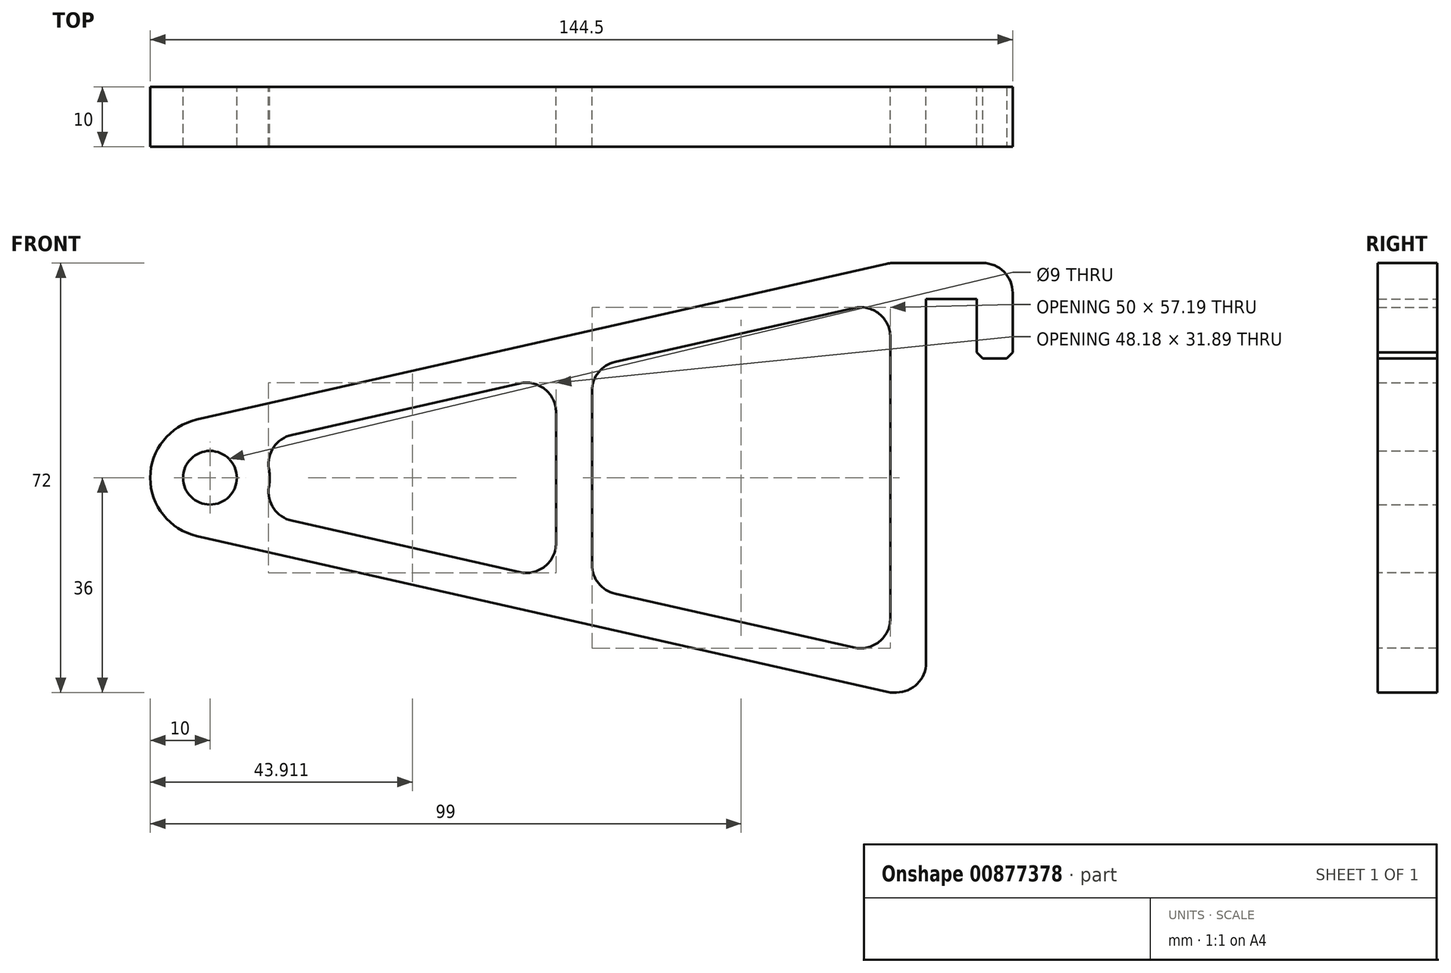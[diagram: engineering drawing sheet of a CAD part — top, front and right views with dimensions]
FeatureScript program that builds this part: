
annotation { "Feature Type Name" : "Feature", "Feature Type Description" : "" }
export const myFeature = defineFeature(function(context is Context, id is Id, definition is map)
    precondition{}
    {
        {
            var Q0;
            Q0=qCreatedBy(makeId("Front.planeOp"),FACE);
            var sketch = newSketch(context, id + "F0", { "sketchPlane" : qUnion([Q0])});
            skLineSegment(sketch, "E0", {"start": v(0, 0) * mm, "end": v(-120, 0) * mm, "construction": true});
            skLineSegment(sketch, "E1", {"start": v(0, 0) * mm, "end": v(0, 30) * mm});
            skLineSegment(sketch, "E2.MirrorCS", {"start": v(0, 0) * mm, "end": v(0, -36) * mm});
            skArc(sketch, "E3", {"start": v(-122.2, 9.75) * mm, "mid": v(-130, 0) * mm, "end": v(-122.2, -9.75) * mm});
            skCircle(sketch, "E4", {"center": v(-120, 0) * mm, "radius": 4.5 * mm});
            skLineSegment(sketch, "E5", {"start": v(0, -36) * mm, "end": v(-6, -36) * mm});
            skLineSegment(sketch, "E6", {"start": v(-6, -36) * mm, "end": v(-122.2, -9.75) * mm});
            skLineSegment(sketch, "E7.MirrorCS", {"start": v(0, 36) * mm, "end": v(-6, 36) * mm});
            skLineSegment(sketch, "E8.MirrorCS", {"start": v(-6, 36) * mm, "end": v(-122.2, 9.75) * mm});
            skLineSegment(sketch, "E9", {"start": v(-6, 29.85) * mm, "end": v(-6, -29.85) * mm});
            skLineSegment(sketch, "E10", {"start": v(-56, 18.56) * mm, "end": v(-56, -18.56) * mm});
            skLineSegment(sketch, "E11.0", {"start": v(-62, 17.2) * mm, "end": v(-62, -17.2) * mm});
            skLineSegment(sketch, "E12.0", {"start": v(-6, 29.85) * mm, "end": v(-56, 18.56) * mm});
            skLineSegment(sketch, "E13.MirrorCS", {"start": v(-6, -29.85) * mm, "end": v(-56, -18.56) * mm});
            skPoint(sketch, "E14.orphan", {"position": v(-120.88, 3.9) * mm});
            skPoint(sketch, "E15.orphan", {"position": v(-120.88, -3.9) * mm});
            skArc(sketch, "E16.trimOffspring", {"start": v(-111.94, -5.92) * mm, "mid": v(-110, 0) * mm, "end": v(-111.94, 5.92) * mm});
            skLineSegment(sketch, "E17.trimOffspring", {"start": v(-62, -17.2) * mm, "end": v(-111.94, -5.92) * mm});
            skLineSegment(sketch, "E18.trimOffspring", {"start": v(-62, 17.2) * mm, "end": v(-111.94, 5.92) * mm});
            skPoint(sketch, "E19.orphan", {"position": v(-4.68, 30.15) * mm});
            skPoint(sketch, "E20.orphan", {"position": v(-4.68, -30.15) * mm});
            skLineSegment(sketch, "E21", {"start": v(0, 36) * mm, "end": v(8.5, 36) * mm});
            skLineSegment(sketch, "E22", {"start": v(8.5, 30) * mm, "end": v(8.5, 20) * mm});
            skLineSegment(sketch, "E23.0", {"start": v(14.5, 36) * mm, "end": v(14.5, 20) * mm});
            skLineSegment(sketch, "E24.0", {"start": v(0, 30) * mm, "end": v(8.5, 30) * mm});
            skLineSegment(sketch, "E25", {"start": v(8.5, 20) * mm, "end": v(14.5, 20) * mm});
            skLineSegment(sketch, "E26", {"start": v(14.5, 36) * mm, "end": v(8.5, 36) * mm});
            skSolve(sketch);
        }
        {
            var Q0;
            Q0 = qSketchRegion(id + "F0", true);
            extrude(context, id + "F1", {"entities" : qUnion([Q0]), "depth" : 10 * mm, "offsetDistance" : 25 * mm});
        }
        {
            var Q0;
            Q0=makeQuery(id+"F1.opExtrude","SWEPT_EDGE",EDGE,{"disambiguationData":[OSD([sQuery(id+"F0.wireOp",EDGE,"E16.trimOffspring"),sQuery(id+"F0.wireOp",EDGE,"E17.trimOffspring")])]});
            var Q1;
            Q1=makeQuery(id+"F1.opExtrude","SWEPT_EDGE",EDGE,{"disambiguationData":[OSD([sQuery(id+"F0.wireOp",EDGE,"E16.trimOffspring"),sQuery(id+"F0.wireOp",EDGE,"E18.trimOffspring")])]});
            var Q2;
            Q2=makeQuery(id+"F1.opExtrude","SWEPT_EDGE",EDGE,{"disambiguationData":[OSD([sQuery(id+"F0.wireOp",EDGE,"E11.0"),sQuery(id+"F0.wireOp",EDGE,"E17.trimOffspring")])]});
            var Q3;
            Q3=makeQuery(id+"F1.opExtrude","SWEPT_EDGE",EDGE,{"disambiguationData":[OSD([sQuery(id+"F0.wireOp",EDGE,"E10"),sQuery(id+"F0.wireOp",EDGE,"E12.0")])]});
            var Q4;
            Q4=makeQuery(id+"F1.opExtrude","SWEPT_EDGE",EDGE,{"disambiguationData":[OSD([sQuery(id+"F0.wireOp",EDGE,"E10"),sQuery(id+"F0.wireOp",EDGE,"E13.MirrorCS")])]});
            var Q5;
            Q5=makeQuery(id+"F1.opExtrude","SWEPT_EDGE",EDGE,{"disambiguationData":[OSD([sQuery(id+"F0.wireOp",EDGE,"E11.0"),sQuery(id+"F0.wireOp",EDGE,"E18.trimOffspring")])]});
            var Q6;
            Q6=makeQuery(id+"F1.opExtrude","SWEPT_EDGE",EDGE,{"disambiguationData":[OSD([sQuery(id+"F0.wireOp",EDGE,"E9"),sQuery(id+"F0.wireOp",EDGE,"E12.0")])]});
            var Q7;
            Q7=makeQuery(id+"F1.opExtrude","SWEPT_EDGE",EDGE,{"disambiguationData":[OSD([sQuery(id+"F0.wireOp",EDGE,"E9"),sQuery(id+"F0.wireOp",EDGE,"E13.MirrorCS")])]});
            var Q8;
            Q8=makeQuery(id+"F1.opExtrude","SWEPT_EDGE",EDGE,{"disambiguationData":[OSD([sQuery(id+"F0.wireOp",EDGE,"E23.0"),sQuery(id+"F0.wireOp",EDGE,"E26")])]});
            var Q9;
            Q9=makeQuery(id+"F1.opExtrude","SWEPT_EDGE",EDGE,{"disambiguationData":[OSD([sQuery(id+"F0.wireOp",EDGE,"E2.MirrorCS"),sQuery(id+"F0.wireOp",EDGE,"E5")])]});
            var Q10;
            Q10=makeQuery(id+"F1.opExtrude","SWEPT_EDGE",EDGE,{"disambiguationData":[OSD([sQuery(id+"F0.wireOp",EDGE,"E7.MirrorCS"),sQuery(id+"F0.wireOp",EDGE,"E8.MirrorCS")])]});
            fillet(context, id + "F2", {"entities" : qUnion([Q0, Q1, Q2, Q3, Q4, Q5, Q6, Q7, Q8, Q9, Q10]), "radius" : 5 * mm, "tangentPropagation" : true, "allowEdgeOverflow" : false});
        }
        {
            var Q0;
            Q0=makeQuery(id+"F1.opExtrude","SWEPT_EDGE",EDGE,{"disambiguationData":[OSD([sQuery(id+"F0.wireOp",EDGE,"E22"),sQuery(id+"F0.wireOp",EDGE,"E25")])]});
            var Q1;
            Q1=makeQuery(id+"F1.opExtrude","SWEPT_EDGE",EDGE,{"disambiguationData":[OSD([sQuery(id+"F0.wireOp",EDGE,"E23.0"),sQuery(id+"F0.wireOp",EDGE,"E25")])]});
            chamfer(context, id + "F3", {"entities" : qUnion([Q0, Q1]), "width" : 1 * mm, "tangentPropagation" : true});
        }
    });
